# Revit family: STL23444_27
name_source: partatom
category: Luminárias
units: mm (PartAtom-declared; Revit-internal decimal feet)

## family parameters
Com base no plano de trabalho = Não
Compartilhado = Não
Corte com vazios quando carregada = Não
Cota do conector redondo = Utilizar diâmetro
Fonte luminosa = Sim
Manter orientação da anotação = Não
Ponto de cálculo do ambiente = Não
Sempre na vertical = Sim
Tipo de parte = Normal

## types (1)
- STL23444/27 - BIVOLT - 2700K - 950lm - 24°
    Altura = 0.07 m
    Arquivo de rede fotométrica = STELLA - STL23444-27 - AR111 ECO 24°.ies
    Dimerização = Não dimerizável
    Diâmetro = 0.11 m
    Elevação padrão = 0 m
    Fabricante = Stella
    Filtro de cor = 16777215
    Fluxo Luminoso = 950 lm
    Grau de proteção (IP) = IP20
    IRC (Índice de reprodução de cores) = >80
    Modelo = Lâmpada LED AR111 24° ECO
    Potência = 11 W
    Referência = STL23444/27
    Temperatura da cor (K) = 2700 K
    Tensão Elétrica = 100V-240V
    Troca de temperatura da cor de lâmpada com esmaecimento = <Nenhum>
    URL = https://stella.com.br
    Ângulo de Abertura = 24º
    Ângulo de inclinação = 90.00°
